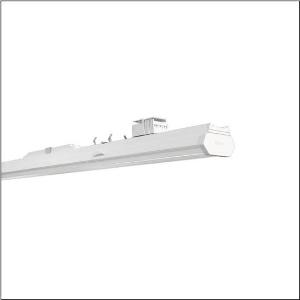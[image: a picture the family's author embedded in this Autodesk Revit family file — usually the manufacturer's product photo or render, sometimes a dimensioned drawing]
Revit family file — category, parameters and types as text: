
# Revit family: licross_r__11_protected_mo_51tp117n485g_c591
name_source: partatom
category: Lighting Fixtures
units: mm (PartAtom-declared; Revit-internal decimal feet)

## family parameters
Cut with Voids When Loaded = No
Host = Face
Light Source = No
Part Type = Normal
Room Calculation Point = No
Round Connector Dimension = Use Diameter
Shared = No

## types (1)
- Licross® 11 Protected MO (1 x LED, 8680 lm, 48.6 W, 4000K)
    Apparent Load = 49 VA
    CIE Flux Codes = 83 94 98 100 100
    Color Rendering = 80
    Color Temperature = 4000K
    Default Elevation = 1800 mm
    Description = Licross® 11 Protected MO, luminaire insert, of sheet steel, galvanised, coil coated, white, length: 1.500mm, width: 90mm, height: 101mm, LED rated luminous flux: 8.680lm, light colour: 840, control gear: ON/OFF, with plug, 3-pole, with phase selection, mains connection: 220..240V, AC, 50/60Hz, rated input power: 49W, halogen-free wiring, primary light control with lens, of plastic, primary optical cover: cover, of PMMA, light emission: direct distribution, primary light characteristic: symmetric, protection rating (complete): IP64, insulation class (complete): insulation class I (protective earthing), certification: CE, ENEC, VDE, UKCA, protection symbol: D if used in an environment with conductive dust loads with corresponding accessories, impact resistance: IK06, permissible ambient temperature for indoor applications: -25..+35°C, corresponds to IFS (International Featured Standards) requirements for safety and quality in the food industry, reducing of maximum allowable ambient temperature of 5°C with ceiling mounting, LABS conformity tested according to VDMA 24364:2018-05, packaging unit: 1 piece
    Height = 92 mm
    Lamp = 1 x LED
    Lamp Light Flux = 8680 lm
    Lamp Power = 48.6 W
    Lamp count = 1
    Length = 1500 mm
    Luminous efficacy = 179 lm/W
    Manufacturer = Siteco
    ModVariant = No
    Model = 51TP117N485G
    Mounting Place = Ceiling
    Mounting Type = Pendant
    Number of Poles = 1
    OnlyDefault = Yes
    Power Factor = 1
    Product Name = Licross® 11 Protected MO
    Product group = luminaire insert
    ProductGroupID = 901
    Protection Class = Protection class I
    Protection Degree = IP 64
    RLX_Detail_Level = 1
    RLX_Emergency_Light_Flux = 0 lm
    RLX_Emergency_Type = 0
    RLX_Emergency_Type_DB = No
    RlxData = <blob elided: 20373 chars, md5=bd9d968e>
    Socket = socket
    Standby Power = 0 W
    System Light Flux = 8680 lm
    System Power = 49 W
    Type Comments = Product without accessories
    Type Image = l_1256148.jpg
    URL = http://relux.com
    VarID = ---
    Voltage = 0 V
    Weight = 0.00 kg
    Width = 88 mm

## geometry (parser evidence)
native form markers: Blend x4, Sweep x10
no freeform markers — native parametric forms only
